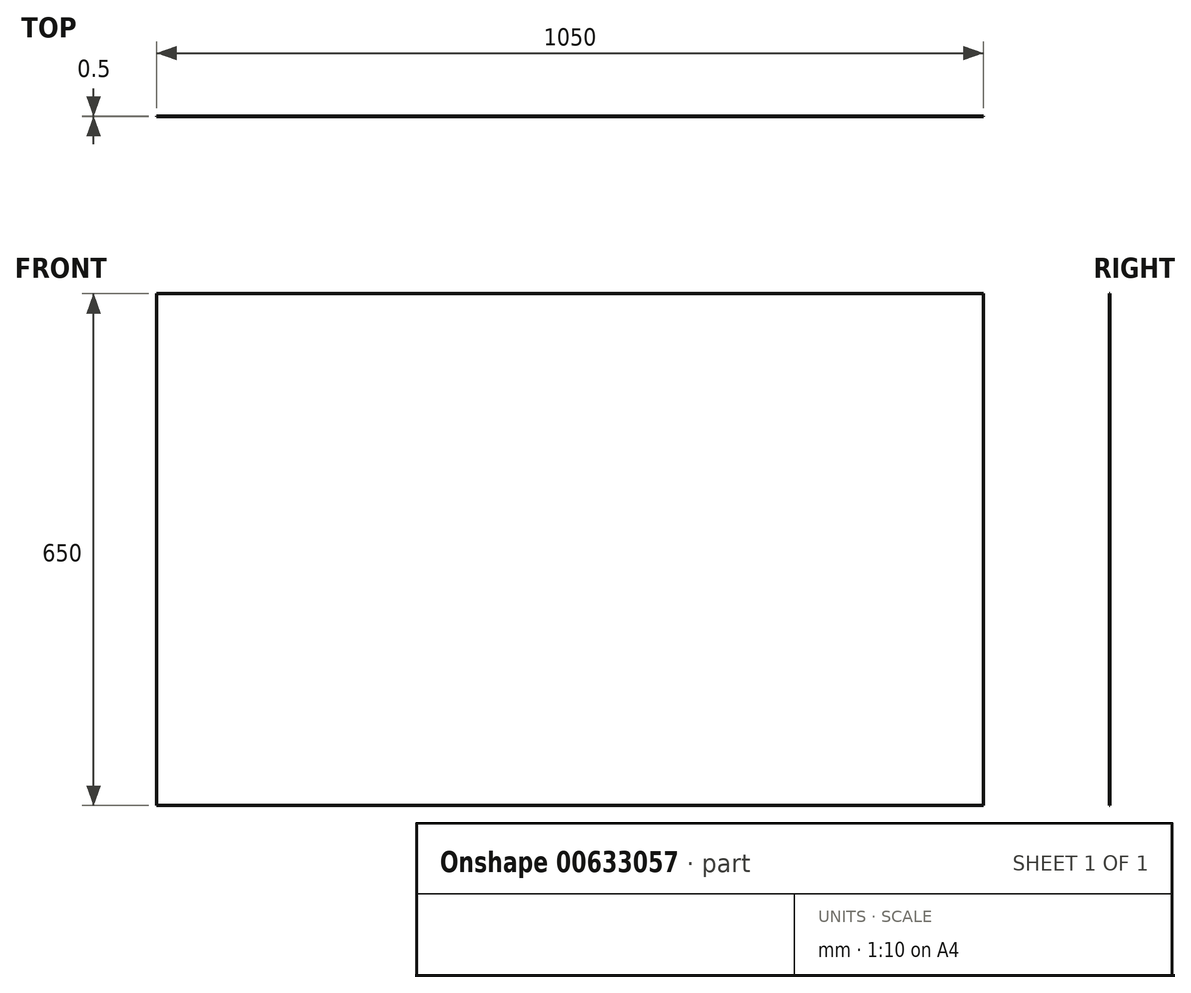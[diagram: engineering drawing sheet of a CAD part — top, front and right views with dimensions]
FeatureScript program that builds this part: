
annotation { "Feature Type Name" : "Feature", "Feature Type Description" : "" }
export const myFeature = defineFeature(function(context is Context, id is Id, definition is map)
    precondition{}
    {
        {
            var Q0;
            Q0=qCreatedBy(makeId("Front.planeOp"),FACE);
            var sketch = newSketch(context, id + "F0", { "sketchPlane" : qUnion([Q0])});
            skLineSegment(sketch, "E0.bottom", {"start": v(0, 0) * mm, "end": v(1050, 0) * mm});
            skLineSegment(sketch, "E0.top", {"start": v(0, 650) * mm, "end": v(1050, 650) * mm});
            skLineSegment(sketch, "E0.left", {"start": v(0, 0) * mm, "end": v(0, 650) * mm});
            skLineSegment(sketch, "E0.right", {"start": v(1050, 0) * mm, "end": v(1050, 650) * mm});
            skSolve(sketch);
        }
        {
            var Q0;
            Q0=makeQuery(id+"F0.imprint","IMPRINT",FACE,{"disambiguationData":[TD([[makeQuery(id+"F0.imprint","IMPRINT",EDGE,{"derivedFrom":sQuery(id+"F0.wireOp",EDGE,"E0.bottom")}),1.0]])]});
            extrude(context, id + "F1", {"entities" : qUnion([Q0]), "depth" : 0.5 * mm, "offsetDistance" : 25 * mm});
        }
    });
